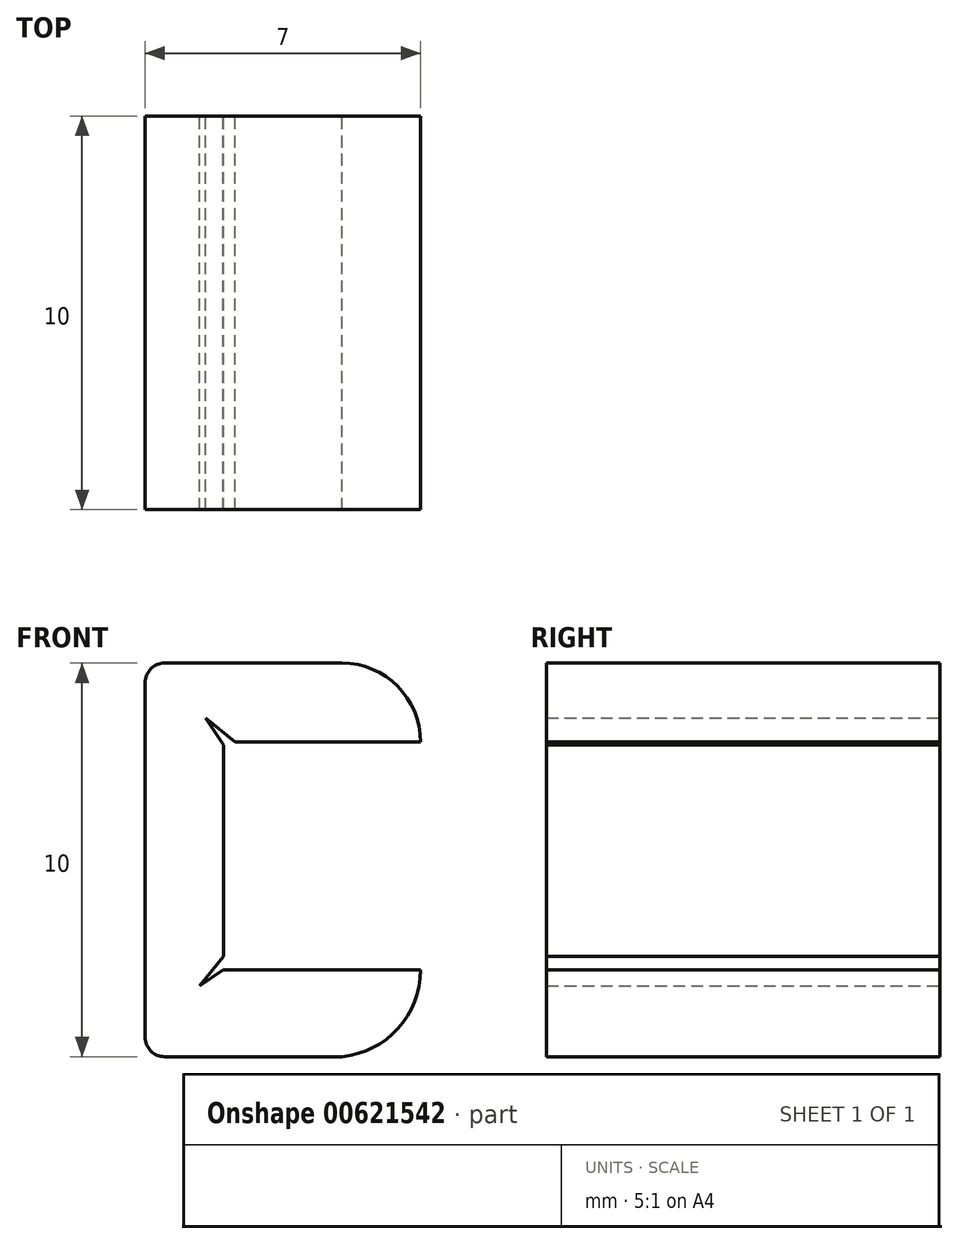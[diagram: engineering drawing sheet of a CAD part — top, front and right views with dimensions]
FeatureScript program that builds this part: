
annotation { "Feature Type Name" : "Feature", "Feature Type Description" : "" }
export const myFeature = defineFeature(function(context is Context, id is Id, definition is map)
    precondition{}
    {
        {
            var Q0;
            Q0=qCreatedBy(makeId("Front.planeOp"),FACE);
            var sketch = newSketch(context, id + "F0", { "sketchPlane" : qUnion([Q0])});
            skLineSegment(sketch, "E0.bottom", {"start": v(0, 0) * mm, "end": v(5, 0) * mm});
            skLineSegment(sketch, "E0.top", {"start": v(0, 5.8) * mm, "end": v(5, 5.8) * mm});
            skLineSegment(sketch, "E0.left", {"start": v(0, 0) * mm, "end": v(0, 5.8) * mm});
            skLineSegment(sketch, "E0.right", {"start": v(5, 0) * mm, "end": v(5, 5.8) * mm});
            skLineSegment(sketch, "E1.bottom", {"start": v(5, 7.8) * mm, "end": v(-1.5, 7.8) * mm});
            skLineSegment(sketch, "E1.top", {"start": v(5, -2.2) * mm, "end": v(-1.5, -2.2) * mm});
            skLineSegment(sketch, "E1.left", {"start": v(5, 7.8) * mm, "end": v(5, -2.2) * mm});
            skLineSegment(sketch, "E1.right", {"start": v(-2, 7.3) * mm, "end": v(-2, -1.7) * mm});
            skArc(sketch, "E2", {"start": v(5, 5.8) * mm, "mid": v(4.42, 7.21) * mm, "end": v(3, 7.8) * mm});
            skArc(sketch, "E3", {"start": v(5, 0) * mm, "mid": v(4.43, -1.48) * mm, "end": v(3, -2.2) * mm});
            skLineSegment(sketch, "E4", {"start": v(0, 0.35) * mm, "end": v(-0.62, -0.4) * mm});
            skLineSegment(sketch, "E5", {"start": v(-0.62, -0.4) * mm, "end": v(-0.02, 0) * mm});
            skLineSegment(sketch, "E6", {"start": v(0, 0) * mm, "end": v(-0.02, 0) * mm});
            skLineSegment(sketch, "E7", {"start": v(0, 5.72) * mm, "end": v(-0.46, 6.4) * mm});
            skLineSegment(sketch, "E8", {"start": v(-0.46, 6.4) * mm, "end": v(0.28, 5.8) * mm});
            skLineSegment(sketch, "E9", {"start": v(0.28, 5.8) * mm, "end": v(0, 5.8) * mm});
            skPoint(sketch, "E10.visualSharp", {"position": v(-2, 7.8) * mm});
            skArc(sketch, "E10.filletArc", {"start": v(-1.5, 7.8) * mm, "mid": v(-1.85, 7.65) * mm, "end": v(-2, 7.3) * mm});
            skPoint(sketch, "E11.visualSharp", {"position": v(-2, -2.2) * mm});
            skArc(sketch, "E11.filletArc", {"start": v(-2, -1.7) * mm, "mid": v(-1.85, -2.05) * mm, "end": v(-1.5, -2.2) * mm});
            skSolve(sketch);
        }
        {
            var Q0;
            Q0=makeQuery(id+"F0.imprint","IMPRINT",FACE,{"disambiguationData":[TD([[makeQuery(id+"F0.imprint","IMPRINT",EDGE,{"derivedFrom":sQuery(id+"F0.wireOp",EDGE,"E0.bottom")}),-1.0]])]});
            extrude(context, id + "F1", {"entities" : qUnion([Q0]), "endBound" : BoundingType.SYMMETRIC, "depth" : 10 * mm, "offsetDistance" : 25 * mm});
        }
    });
